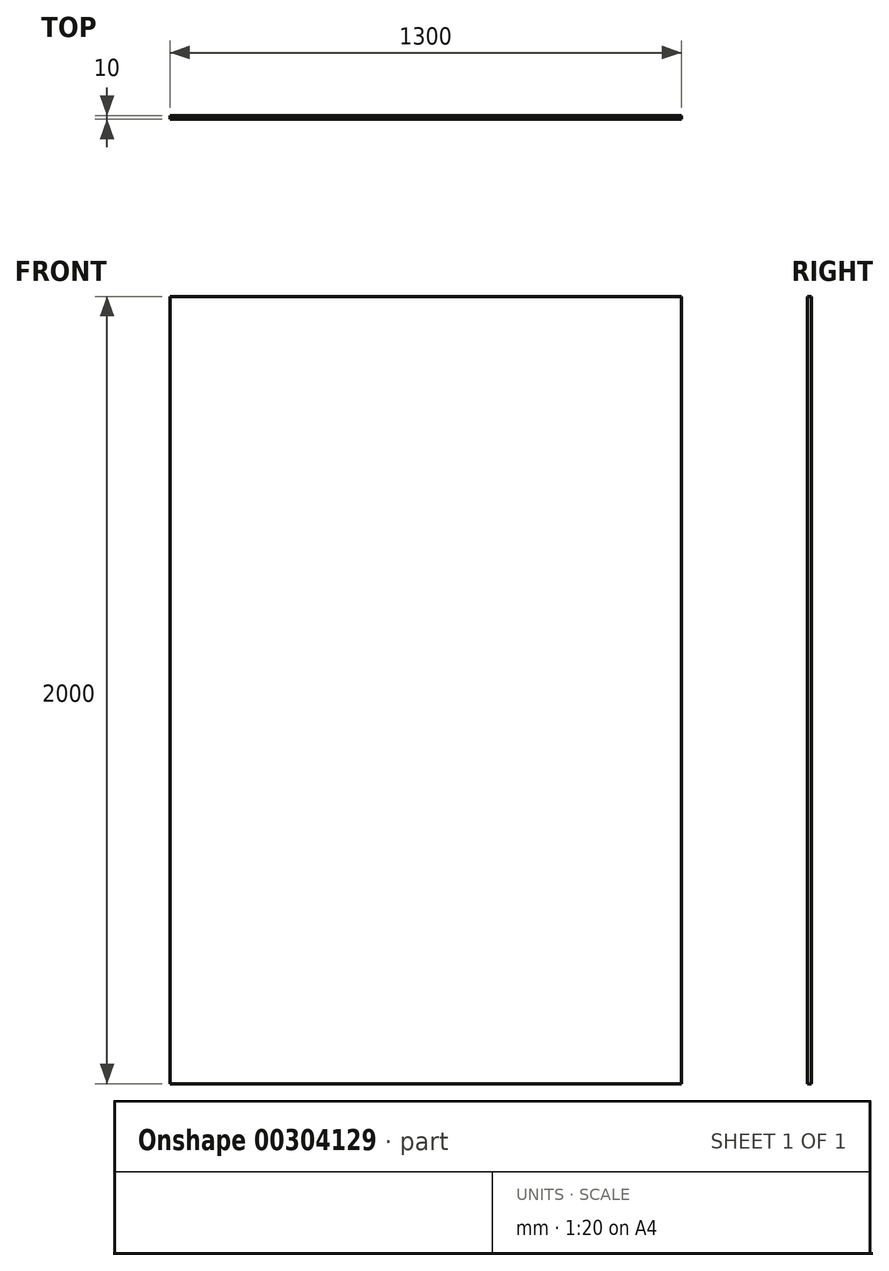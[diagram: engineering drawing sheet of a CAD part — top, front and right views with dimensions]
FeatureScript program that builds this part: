
annotation { "Feature Type Name" : "Feature", "Feature Type Description" : "" }
export const myFeature = defineFeature(function(context is Context, id is Id, definition is map)
    precondition{}
    {
        {
            var Q0;
            Q0=qCreatedBy(makeId("Top.planeOp"),FACE);
            var sketch = newSketch(context, id + "F0", { "sketchPlane" : qUnion([Q0])});
            skLineSegment(sketch, "E0.bottom", {"start": v(-208.69, 8.8) * mm, "end": v(1091.31, 8.8) * mm});
            skLineSegment(sketch, "E0.top", {"start": v(-208.69, -1.2) * mm, "end": v(1091.31, -1.2) * mm});
            skLineSegment(sketch, "E0.left", {"start": v(-208.69, 8.8) * mm, "end": v(-208.69, -1.2) * mm});
            skLineSegment(sketch, "E0.right", {"start": v(1091.31, 8.8) * mm, "end": v(1091.31, -1.2) * mm});
            skSolve(sketch);
        }
        {
            var Q0;
            Q0=makeQuery(id+"F0.imprint","IMPRINT",FACE,{"disambiguationData":[TD([[makeQuery(id+"F0.imprint","IMPRINT",EDGE,{"derivedFrom":sQuery(id+"F0.wireOp",EDGE,"E0.bottom")}),-1.0]])]});
            extrude(context, id + "F1", {"entities" : qUnion([Q0]), "depth" : 2000 * mm, "offsetDistance" : 25 * mm});
        }
    });
